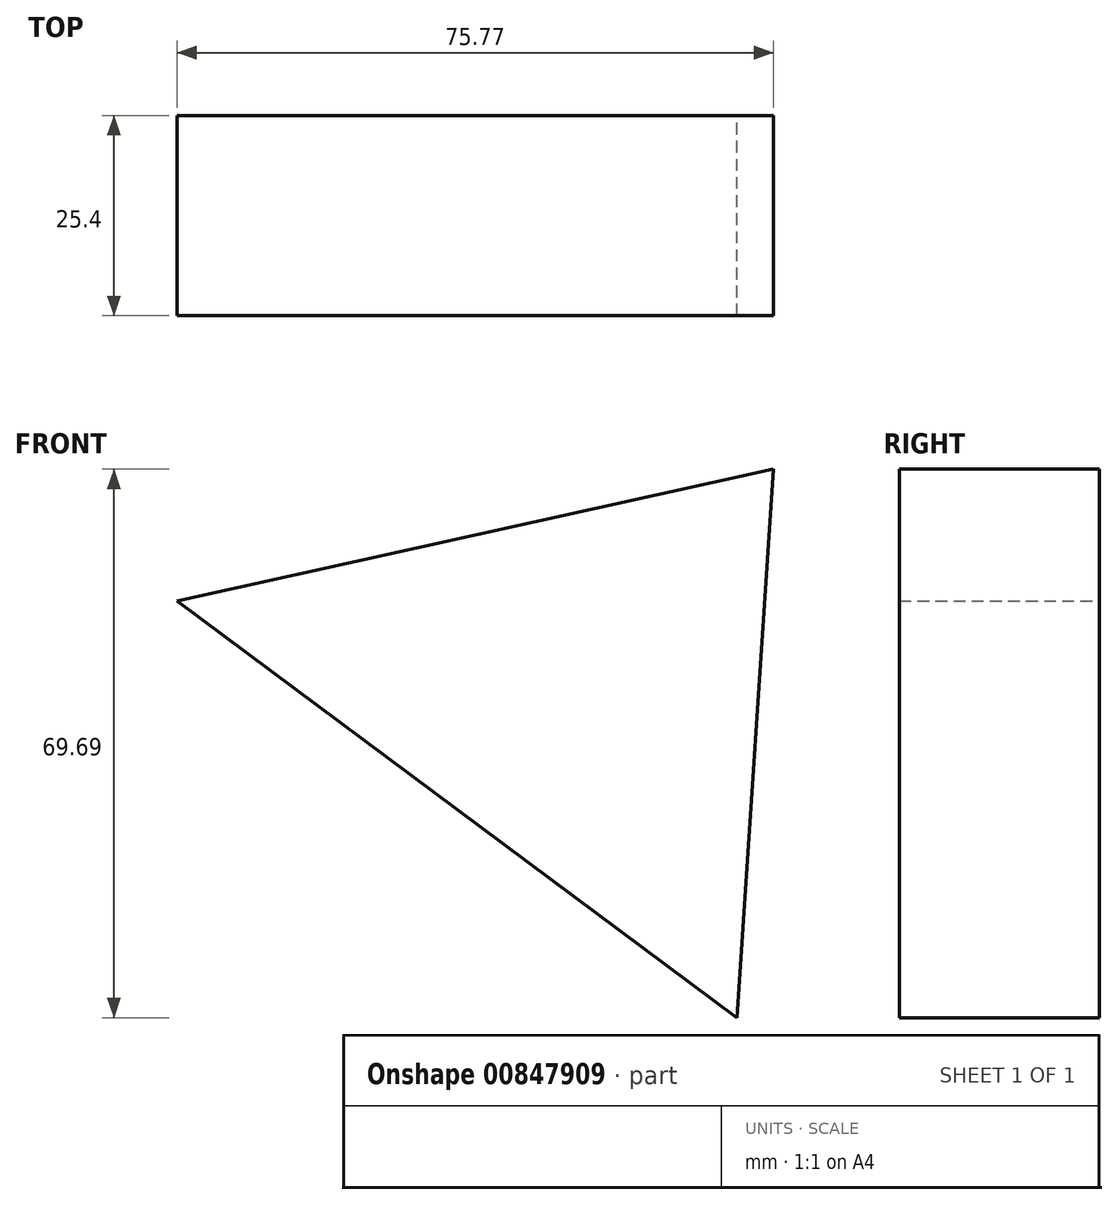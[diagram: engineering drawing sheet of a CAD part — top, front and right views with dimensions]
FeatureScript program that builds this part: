
annotation { "Feature Type Name" : "Feature", "Feature Type Description" : "" }
export const myFeature = defineFeature(function(context is Context, id is Id, definition is map)
    precondition{}
    {
        {
            var Q0;
            Q0=qCreatedBy(makeId("Front.planeOp"),FACE);
            var sketch = newSketch(context, id + "F0", { "sketchPlane" : qUnion([Q0])});
            skLineSegment(sketch, "E0", {"start": v(-38.07, 21.66) * mm, "end": v(37.7, 38.44) * mm});
            skLineSegment(sketch, "E1", {"start": v(37.7, 38.44) * mm, "end": v(33.1, -31.25) * mm});
            skLineSegment(sketch, "E2", {"start": v(33.1, -31.25) * mm, "end": v(-38.07, 21.66) * mm});
            skSolve(sketch);
        }
        {
            var Q0;
            Q0=makeQuery(id+"F0.imprint","IMPRINT",FACE,{"disambiguationData":[TD([[makeQuery(id+"F0.imprint","IMPRINT",EDGE,{"derivedFrom":sQuery(id+"F0.wireOp",EDGE,"E0")}),-1.0]])]});
            extrude(context, id + "F1", {"entities" : qUnion([Q0]), "depth" : 25.4 * mm, "offsetDistance" : 25.4 * mm});
        }
    });
